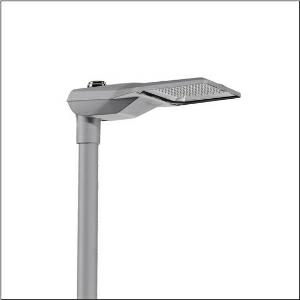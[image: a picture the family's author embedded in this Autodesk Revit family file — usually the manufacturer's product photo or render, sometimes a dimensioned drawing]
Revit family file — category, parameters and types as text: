
# Revit family: streetlight_sl_21_midi___st0_8a_5xe7c37n08nb_761f
name_source: partatom
category: Lighting Fixtures
units: mm (PartAtom-declared; Revit-internal decimal feet)

## family parameters
Cut with Voids When Loaded = No
Host = Face
Light Source = No
Part Type = Normal
Room Calculation Point = No
Round Connector Dimension = Use Diameter
Shared = No

## types (1)
- --- (1 x LED, 22700 lm, 151.2 W, 3000K)
    Apparent Load = 151 VA
    CIE Flux Codes = 41 75 97 100 100
    Color Rendering = 70
    Color Temperature = 3000K
    Default Elevation = 1800 mm
    Description = Streetlight SL 21 midi, mast luminaire, primary light control with lens, of PMMA, primary optical cover: cover, of toughened safety glass, transparent, light distribution: ST0.8a, light emission: direct distribution, primary light characteristic: asymmetric, installation type: side-entry, LED, 3G 2.5mm², High Power LED, rated luminous flux: 22.700lm, luminous efficacy: 150lm/W, light colour: 730, colour temperature: 3000K, control gear: NEMA (7pin), control: overheat protection, pre-setting: linear dimming characteristic, constant luminous flux control, time-dependent luminous flux control, flexible luminous flux parameterisation, mains connection: 220..240V, AC, 50/60Hz, connection cable pre-assembled, cable length: 12,5m, wiring characteristics: H05VV-F, start of lifetime: 151W, end of service life: 157W, reduction: 70W, luminaire housing, of diecast aluminium (EN AC-44300), powder-coated, Siteco® metallic grey (DB 702S), corrosivity category C5 mid according to DIN EN ISO 12944, multi-level sealing system, sealing non-destructively replaceable, inclination adjustable: 0°, 5°, 10°, 15°, length: 644mm, width: 335mm, height: 110mm, spigot size: 42mm (side-entry), mounting height: 4..8m, protection rating (complete): IP66, insulation class (complete): insulation class I (protective earthing), certification: CE, ENEC, ENEC+, VDE, impact resistance: IK10, permissible operating ambient temperature for outdoor applications: -40..+50°C, standard-compliant lighting for roads and squares, packaging unit: 1 piece

Light Distribution: ST0.8a
    Height = 111 mm
    Lamp = 1 x LED
    Lamp Light Flux = 22700 lm
    Lamp Power = 151.2 W
    Lamp count = 1
    Length = 644 mm
    Luminous efficacy = 150 lm/W
    Manufacturer = Siteco
    ModVariant = No
    Model = 5XE7C37N08NB
    Number of Poles = 1
    OnlyDefault = Yes
    Power Factor = 1
    Product Name = Streetlight SL 21 midi | ST0.8a
    Product group = mast luminaire | pylon top
    ProductGroupID = 6100
    Protection Class = Protection class I
    Protection Degree = IP 66
    RLX_Detail_Level = 1
    RLX_Emergency_Light_Flux = 0 lm
    RLX_Emergency_Type = 0
    RLX_Emergency_Type_DB = No
    RlxData = <blob elided: 26609 chars, md5=3b72299b>
    Socket = socket
    Standby Power = 0 W
    System Light Flux = 22700 lm
    System Power = 151 W
    Type Comments = factory setting: luminous flux: 100 % | dim-lin: 254 | 802 mA
    Type Image = l_1294377.jpg
    URL = http://relux.com
    VarID = @adj_133874
    Voltage = 0 V
    Weight = 0.00 kg
    Width = 336 mm

## geometry (parser evidence)
native form markers: Blend x4, Sweep x11
no freeform markers — native parametric forms only
